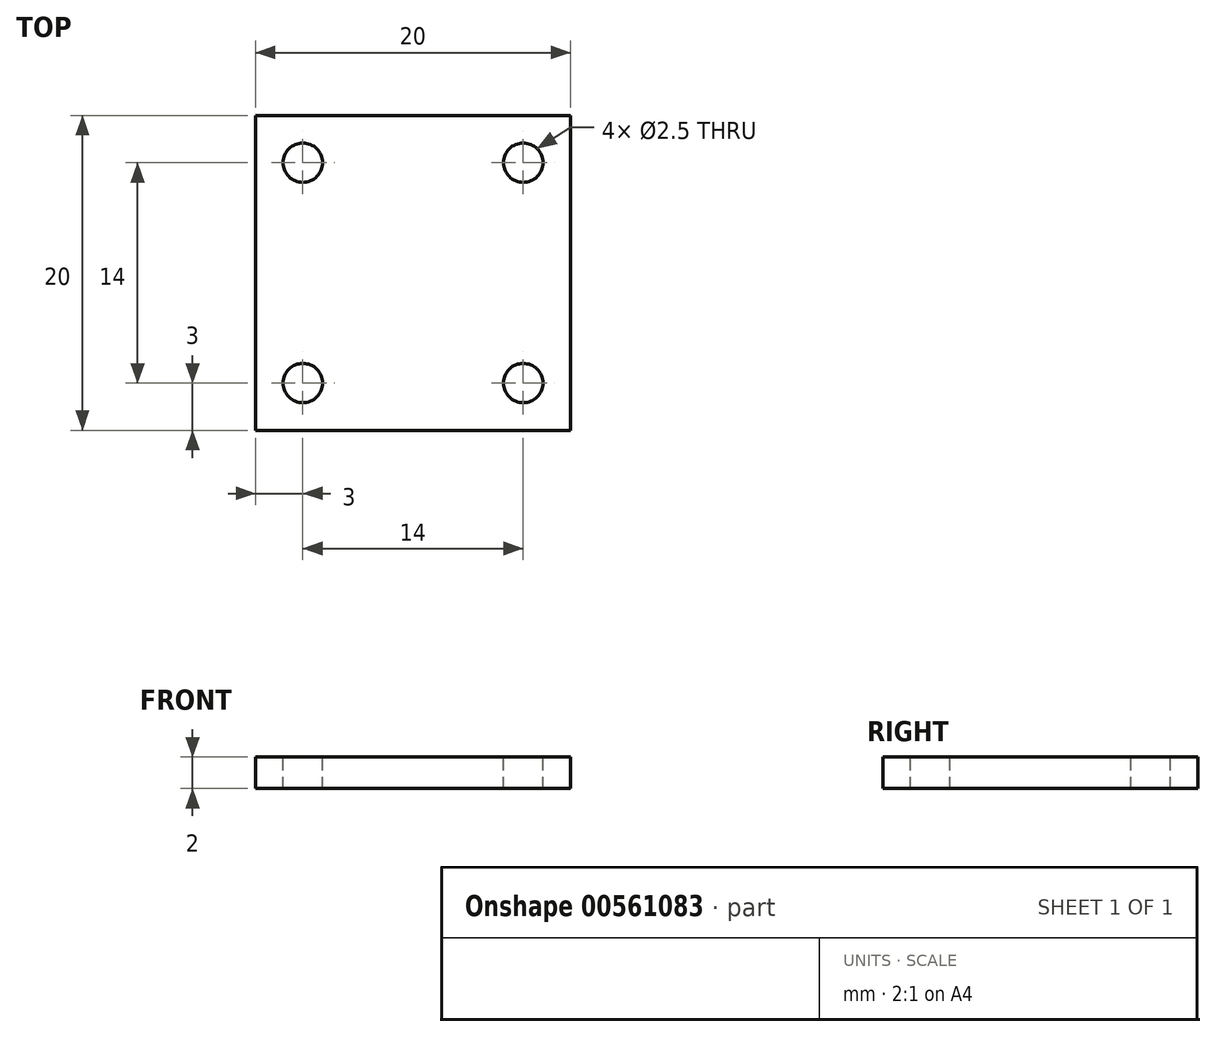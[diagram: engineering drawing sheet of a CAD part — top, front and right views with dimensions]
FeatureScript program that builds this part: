
annotation { "Feature Type Name" : "Feature", "Feature Type Description" : "" }
export const myFeature = defineFeature(function(context is Context, id is Id, definition is map)
    precondition{}
    {
        {
            var Q0;
            Q0=qCreatedBy(makeId("Top.planeOp"),FACE);
            var sketch = newSketch(context, id + "F0", { "sketchPlane" : qUnion([Q0])});
            skLineSegment(sketch, "E0.bottom", {"start": v(-10, 10) * mm, "end": v(10, 10) * mm});
            skLineSegment(sketch, "E0.top", {"start": v(-10, -10) * mm, "end": v(10, -10) * mm});
            skLineSegment(sketch, "E0.left", {"start": v(-10, 10) * mm, "end": v(-10, -10) * mm});
            skLineSegment(sketch, "E0.right", {"start": v(10, 10) * mm, "end": v(10, -10) * mm});
            skSolve(sketch);
        }
        {
            var Q0;
            Q0=makeQuery(id+"F0.imprint","IMPRINT",FACE,{"disambiguationData":[TD([[makeQuery(id+"F0.imprint","IMPRINT",EDGE,{"derivedFrom":sQuery(id+"F0.wireOp",EDGE,"E0.bottom")}),-1.0]])]});
            extrude(context, id + "F1", {"entities" : qUnion([Q0]), "oppositeDirection" : true, "depth" : 2 * mm, "offsetDistance" : 25 * mm});
        }
        {
            var Q0;
            Q0=makeQuery(id+"F1.opExtrude","CAP_FACE",FACE,{"disambiguationData":[OSD([sQuery(id+"F0.wireOp",EDGE,"E0.bottom"),sQuery(id+"F0.wireOp",EDGE,"E0.top"),sQuery(id+"F0.wireOp",EDGE,"E0.left"),sQuery(id+"F0.wireOp",EDGE,"E0.right")])],"isStart":true});
            var sketch = newSketch(context, id + "F2", { "sketchPlane" : qUnion([Q0])});
            skPoint(sketch, "E1", {"position": v(-7, 7) * mm});
            skPoint(sketch, "E2", {"position": v(7, 7) * mm});
            skLineSegment(sketch, "E3", {"start": v(-11.27, 0) * mm, "end": v(14.07, 0) * mm});
            skPoint(sketch, "E3.startSnap0", {"position": v(-10, 0) * mm});
            skPoint(sketch, "E3.endSnap0", {"position": v(10, 0) * mm});
            skPoint(sketch, "E4.MirrorP", {"position": v(-7, -7) * mm});
            skPoint(sketch, "E5.MirrorP", {"position": v(7, -7) * mm});
            skSolve(sketch);
        }
        {
            var Q0;
            Q0=sQuery(id+"F2.wireOp",VERTEX,"E1");
            var Q1;
            Q1=sQuery(id+"F2.wireOp",VERTEX,"E2");
            var Q2;
            Q2=sQuery(id+"F2.wireOp",VERTEX,"E4.MirrorP");
            var Q3;
            Q3=sQuery(id+"F2.wireOp",VERTEX,"E5.MirrorP");
            var Q4;
            Q4=makeQuery(id+"F1.opExtrude","SWEPT_BODY",BODY,{"disambiguationData":[OSD([sQuery(id+"F0.wireOp",EDGE,"E0.bottom"),sQuery(id+"F0.wireOp",EDGE,"E0.top"),sQuery(id+"F0.wireOp",EDGE,"E0.left"),sQuery(id+"F0.wireOp",EDGE,"E0.right")])]});
            hole(context, id + "F3", {"style" : HoleStyle.SIMPLE, "endStyle" : HoleEndStyle.THROUGH, "standardTappedOrClearance" : lookupTablePath({ "standard" : "ISO", "engagement" : "75%", "pitch" : "0.5 mm", "size" : "M3", "type" : "Tapped" }), "standardBlindInLast" : lookupTablePath({ "standard" : "ISO", "engagement" : "75%", "pitch" : "0.5 mm", "size" : "M3", "type" : "Tapped" }), "holeDiameter" : 2.5 * mm, "showTappedDepth" : true, "isTappedThrough" : true, "tappedDepth" : 12 * mm, "tapClearance" : 3, "startFromSketch" : true, "locations" : qUnion([Q0, Q1, Q2, Q3]), "scope" : qUnion([Q4]), "majorDiameter" : 3 * mm});
        }
    });
